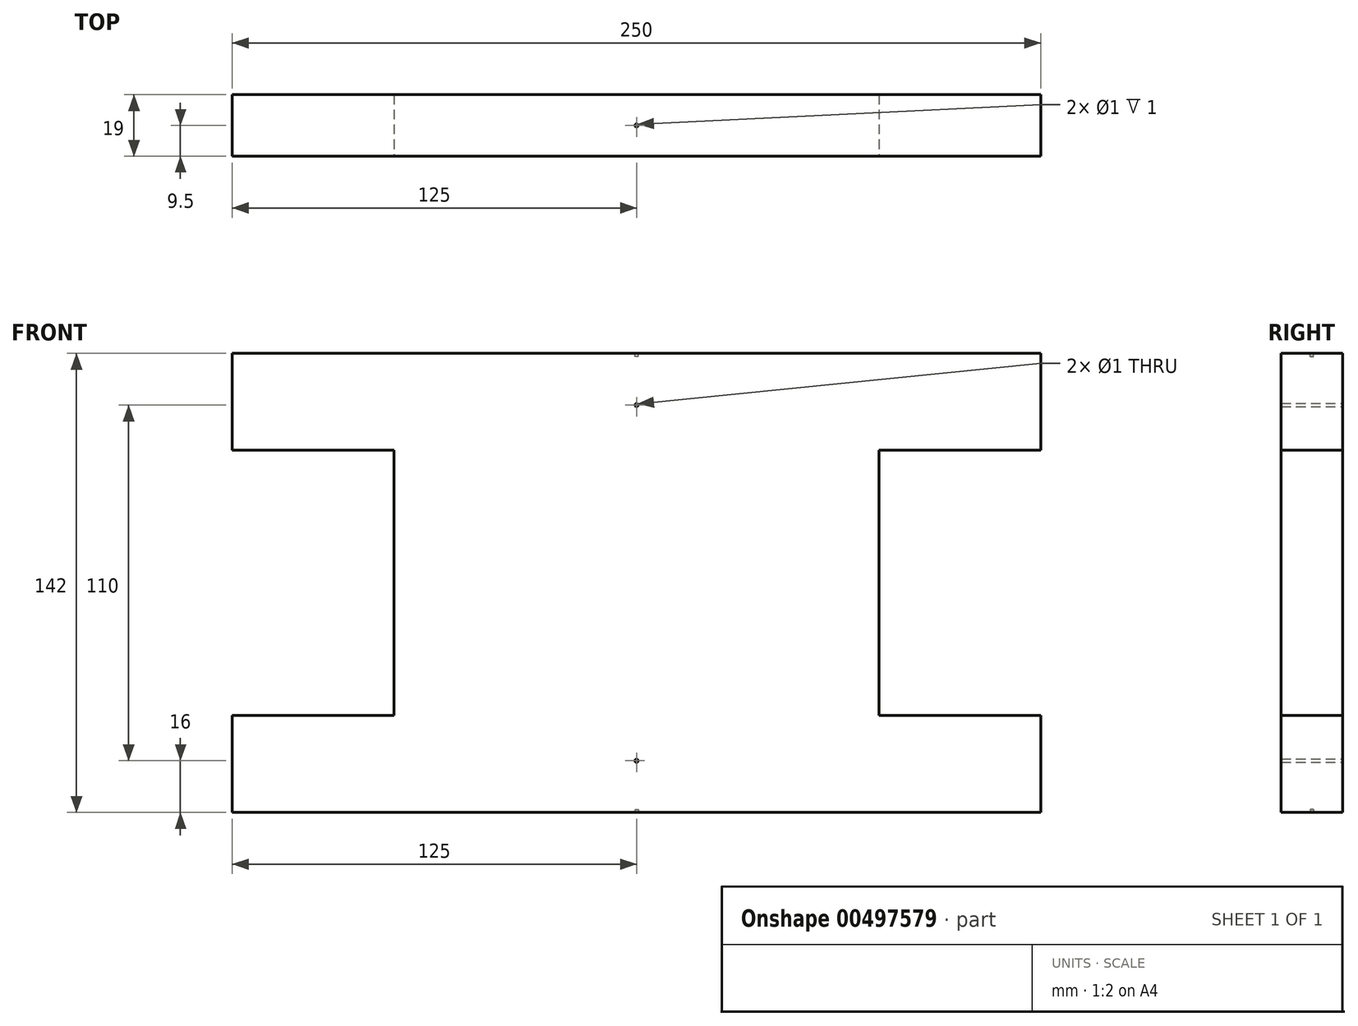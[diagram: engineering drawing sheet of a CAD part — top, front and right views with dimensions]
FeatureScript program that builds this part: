
annotation { "Feature Type Name" : "Feature", "Feature Type Description" : "" }
export const myFeature = defineFeature(function(context is Context, id is Id, definition is map)
    precondition{}
    {
        {
            var Q0;
            Q0=qCreatedBy(makeId("Front.planeOp"),FACE);
            var sketch = newSketch(context, id + "F0", { "sketchPlane" : qUnion([Q0])});
            skLineSegment(sketch, "E0.bottom", {"start": v(0, 0) * mm, "end": v(150, 0) * mm});
            skLineSegment(sketch, "E0.top", {"start": v(0, 142) * mm, "end": v(150, 142) * mm});
            skLineSegment(sketch, "E0.left", {"start": v(0, 0) * mm, "end": v(0, 142) * mm});
            skLineSegment(sketch, "E0.right", {"start": v(150, 0) * mm, "end": v(150, 142) * mm});
            skPoint(sketch, "E1.centerSnap0", {"position": v(75, 142) * mm});
            skLineSegment(sketch, "E2", {"start": v(0, 71) * mm, "end": v(150, 71) * mm, "construction": true});
            skCircle(sketch, "E3", {"center": v(75, 16) * mm, "radius": 0.5 * mm});
            skPoint(sketch, "E3.centerSnap0", {"position": v(75, 71) * mm});
            skCircle(sketch, "E4.MirrorC", {"center": v(75, 126) * mm, "radius": 0.5 * mm});
            skSolve(sketch);
        }
        {
            var Q0;
            Q0 = qSketchRegion(id + "F0", true);
            extrude(context, id + "F1", {"entities" : qUnion([Q0]), "depth" : 19 * mm, "offsetDistance" : 25.4 * mm});
        }
        {
            var Q0;
            Q0=makeQuery(id+"F1.opExtrude","SWEPT_FACE",FACE,{"disambiguationData":[OSD([sQuery(id+"F0.wireOp",EDGE,"E0.bottom")])]});
            var sketch = newSketch(context, id + "F2", { "sketchPlane" : qUnion([Q0])});
            skCircle(sketch, "E5", {"center": v(75, 9.5) * mm, "radius": 0.5 * mm});
            skPoint(sketch, "E5.centerSnap0", {"position": v(75, 0) * mm});
            skPoint(sketch, "E5.centerSnap1", {"position": v(0, 9.5) * mm});
            skSolve(sketch);
        }
        {
            var Q0;
            Q0 = qSketchRegion(id + "F2", true);
            extrude(context, id + "F3", {"entities" : qUnion([Q0]), "operationType" : NewBodyOperationType.REMOVE, "oppositeDirection" : true, "depth" : 1 * mm, "offsetDistance" : 25.4 * mm});
        }
        {
            var Q0;
            Q0=makeQuery(id+"F1.opExtrude","SWEPT_FACE",FACE,{"disambiguationData":[OSD([sQuery(id+"F0.wireOp",EDGE,"E0.top")])]});
            var sketch = newSketch(context, id + "F4", { "sketchPlane" : qUnion([Q0])});
            skCircle(sketch, "E6", {"center": v(75, -9.5) * mm, "radius": 0.5 * mm});
            skPoint(sketch, "E6.centerSnap0", {"position": v(75, -19) * mm});
            skPoint(sketch, "E6.centerSnap1", {"position": v(0, -9.5) * mm});
            skSolve(sketch);
        }
        {
            var Q0;
            Q0 = qSketchRegion(id + "F4", true);
            extrude(context, id + "F5", {"entities" : qUnion([Q0]), "operationType" : NewBodyOperationType.REMOVE, "oppositeDirection" : true, "depth" : 1 * mm, "offsetDistance" : 25.4 * mm});
        }
        {
            var Q0;
            Q0=makeQuery(id+"F1.opExtrude","SWEPT_FACE",FACE,{"disambiguationData":[OSD([sQuery(id+"F0.wireOp",EDGE,"E0.left")])]});
            var sketch = newSketch(context, id + "F6", { "sketchPlane" : qUnion([Q0])});
            skLineSegment(sketch, "E7.bottom", {"start": v(0, 142) * mm, "end": v(19, 142) * mm});
            skLineSegment(sketch, "E7.top", {"start": v(0, 112) * mm, "end": v(19, 112) * mm});
            skLineSegment(sketch, "E7.left", {"start": v(0, 142) * mm, "end": v(0, 112) * mm});
            skLineSegment(sketch, "E7.right", {"start": v(19, 142) * mm, "end": v(19, 112) * mm});
            skLineSegment(sketch, "E8", {"start": v(0, 71) * mm, "end": v(19, 71) * mm, "construction": true});
            skLineSegment(sketch, "E9.MirrorCS", {"start": v(0, 0) * mm, "end": v(19, 0) * mm});
            skLineSegment(sketch, "E10.MirrorCS", {"start": v(0, 30) * mm, "end": v(19, 30) * mm});
            skLineSegment(sketch, "E11.MirrorCS", {"start": v(0, 0) * mm, "end": v(0, 30) * mm});
            skLineSegment(sketch, "E12.MirrorCS", {"start": v(19, 0) * mm, "end": v(19, 30) * mm});
            skSolve(sketch);
        }
        {
            var Q0;
            Q0 = qSketchRegion(id + "F6", true);
            extrude(context, id + "F7", {"entities" : qUnion([Q0]), "operationType" : NewBodyOperationType.ADD, "depth" : 50 * mm, "offsetDistance" : 25.4 * mm});
        }
        {
            var Q0;
            Q0=makeQuery(id+"F1.opExtrude","SWEPT_FACE",FACE,{"disambiguationData":[OSD([sQuery(id+"F0.wireOp",EDGE,"E0.right")])]});
            var sketch = newSketch(context, id + "F8", { "sketchPlane" : qUnion([Q0])});
            skLineSegment(sketch, "E13.bottom", {"start": v(0, 0) * mm, "end": v(-19, 0) * mm});
            skLineSegment(sketch, "E13.top", {"start": v(0, 30) * mm, "end": v(-19, 30) * mm});
            skLineSegment(sketch, "E13.left", {"start": v(0, 0) * mm, "end": v(0, 30) * mm});
            skLineSegment(sketch, "E13.right", {"start": v(-19, 0) * mm, "end": v(-19, 30) * mm});
            skLineSegment(sketch, "E14", {"start": v(0, 71) * mm, "end": v(-19, 71) * mm, "construction": true});
            skLineSegment(sketch, "E15.MirrorCS", {"start": v(0, 142) * mm, "end": v(-19, 142) * mm});
            skLineSegment(sketch, "E16.MirrorCS", {"start": v(0, 112) * mm, "end": v(-19, 112) * mm});
            skLineSegment(sketch, "E17.MirrorCS", {"start": v(0, 142) * mm, "end": v(0, 112) * mm});
            skLineSegment(sketch, "E18.MirrorCS", {"start": v(-19, 142) * mm, "end": v(-19, 112) * mm});
            skSolve(sketch);
        }
        {
            var Q0;
            Q0 = qSketchRegion(id + "F8", true);
            extrude(context, id + "F9", {"entities" : qUnion([Q0]), "operationType" : NewBodyOperationType.ADD, "depth" : 50 * mm, "offsetDistance" : 25.4 * mm});
        }
    });
